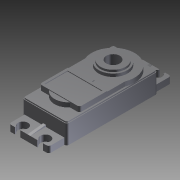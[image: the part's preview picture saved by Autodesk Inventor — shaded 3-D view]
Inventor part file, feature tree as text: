
AUTODESK INVENTOR PART (.ipt)
format: ipt  version: 2015 (Build 190159000, 159)  size: 197,120 bytes
history: native  units: in
note: dims shown in document units (in); Inventor stores cm internally (conversion verified against a paired STEP export)
features: fillet x1, other x1, imported_body x1
ambient origin geometry x8: Origin, YZ Plane, XZ Plane, XY Plane, X Axis, Y Axis, Z Axis, Center Point
bodies: Body1 (feature_tree)
feature tree (3):
  fillet  "Fillet2"  [1 undecoded]
  other  "TOWER PRO MG-995, ANALOG SERVO, BODY, TOP.ipt1"
  imported_body  "Base1"
note: 1 required parameter value undecoded (feature->parameter linkage not recoverable at this tier; creation-order binding heuristic only, values carry confidence <= 0.55)
